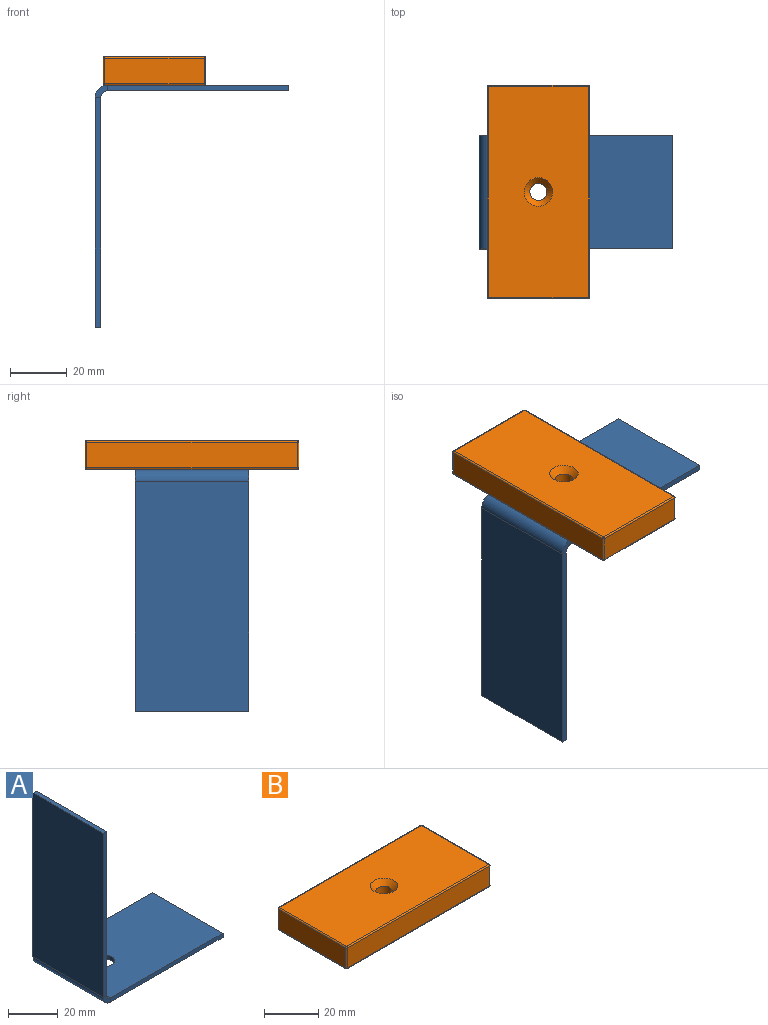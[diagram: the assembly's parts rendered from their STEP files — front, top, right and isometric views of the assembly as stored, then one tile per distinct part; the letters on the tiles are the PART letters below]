
ASSEMBLY  parts=2 mates=1
PART A: 15 faces, bbox 68x40x85 mm
  f0: plane 63.7x2mm, normal (0,1,0), area 127.4mm2, adj f3,f4,f5,f12
  f1: plane 63.7x2mm, normal (0,-1,0), area 127.4mm2, adj f3,f4,f5,f11
  f2: cylinder r=4mm len=8mm, axis (0,0,1), area 50.3mm2, adj f4,f5
  f3: plane 40x2mm, normal (1,0,0), area 80mm2, adj f0,f1,f4,f5
  f4: plane 63.7x40mm, normal (0,0,1), area 2497.7mm2, adj f0,f1,f2,f3,f14
  f5: plane 63.7x40mm, normal (0,0,-1), area 2497.7mm2, adj f0,f1,f2,f3,f13
  f6: plane 80.7x2mm, normal (0,1,0), area 161.4mm2, adj f7,f9,f10,f12
  f7: plane 40x2mm, normal (0,0,1), area 80mm2, adj f6,f8,f9,f10
  f8: plane 80.7x2mm, normal (0,-1,0), area 161.4mm2, adj f7,f9,f10,f11
  f9: plane 80.7x40mm, normal (1,0,0), area 3228mm2, adj f6,f7,f8,f14
  f10: plane 80.7x40mm, normal (-1,0,0), area 3228mm2, adj f6,f7,f8,f13
  f11: plane 4.3x4.3mm, normal (0,-1,0), area 10.4mm2, adj f1,f8,f13,f14
  f12: plane 4.3x4.3mm, normal (0,1,0), area 10.4mm2, adj f0,f6,f13,f14
  f13: cylinder r=4.3mm len=40mm, axis (0,-1,0), area 270.2mm2, adj f5,f10,f11,f12
  f14: cylinder r=2.3mm len=40mm, axis (0,-1,0), area 144.5mm2, adj f4,f9,f11,f12
PART B: 34 faces, bbox 75x36x10 mm
  f0: plane 74x9mm, normal (0,-1,0), area 666mm2, adj f14,f19,f22,f25
  f1: plane 35x9mm, normal (1,0,0), area 315mm2, adj f11,f20,f21,f25
  f2: plane 74x9mm, normal (0,1,0), area 666mm2, adj f6,f10,f11,f12
  f3: plane 35x9mm, normal (-1,0,0), area 315mm2, adj f6,f9,f13,f14
  f4: plane 74x35mm, normal (0,0,1), area 2511.5mm2, adj f9,f10,f19,f20,f33
  f5: plane 74x35mm, normal (0,0,-1), area 2536.6mm2, adj f12,f13,f21,f22,f27,f30,f32
  f6: cylinder r=0.5mm len=9mm, axis (0,0,-1), area 7.1mm2, adj f2,f3,f7,f8
  f7: sphere r=0.5mm, area 0.4mm2, adj f6,f9,f10
  f8: sphere r=0.5mm, area 0.4mm2, adj f6,f12,f13
  f9: cylinder r=0.5mm len=35mm, axis (0,1,0), area 27.5mm2, adj f3,f4,f7,f15
  f10: cylinder r=0.5mm len=74mm, axis (1,0,0), area 58.1mm2, adj f2,f4,f7,f16
  f11: cylinder r=0.5mm len=9mm, axis (0,0,-1), area 7.1mm2, adj f1,f2,f16,f17
  f12: cylinder r=0.5mm len=74mm, axis (-1,0,0), area 58.1mm2, adj f2,f5,f8,f17
  f13: cylinder r=0.5mm len=35mm, axis (0,-1,0), area 27.5mm2, adj f3,f5,f8,f18
  f14: cylinder r=0.5mm len=9mm, axis (0,0,-1), area 7.1mm2, adj f0,f3,f15,f18
  f15: sphere r=0.5mm, area 0.4mm2, adj f9,f14,f19
  f16: sphere r=0.5mm, area 0.4mm2, adj f10,f11,f20
  f17: sphere r=0.5mm, area 0.4mm2, adj f11,f12,f21
  f18: sphere r=0.5mm, area 0.4mm2, adj f13,f14,f22
  f19: cylinder r=0.5mm len=74mm, axis (-1,0,0), area 58.1mm2, adj f0,f4,f15,f23
  f20: cylinder r=0.5mm len=35mm, axis (0,-1,0), area 27.5mm2, adj f1,f4,f16,f23
  f21: cylinder r=0.5mm len=35mm, axis (0,1,0), area 27.5mm2, adj f1,f5,f17,f24
  f22: cylinder r=0.5mm len=74mm, axis (1,0,0), area 58.1mm2, adj f0,f5,f18,f24
  f23: sphere r=0.5mm, area 0.4mm2, adj f19,f20,f25
  f24: sphere r=0.5mm, area 0.4mm2, adj f21,f22,f25
  f25: cylinder r=0.5mm len=9mm, axis (0,0,-1), area 7.1mm2, adj f0,f1,f23,f24
  f26: cylinder r=1.5mm len=7.43mm, axis (0,0,-1), area 70mm2, adj f27,f28
  f27: cone r=1.5mm half-angle=41deg, axis (0,0,-1), area 8.4mm2, adj f5,f26
  f28: cone r=0mm half-angle=59deg, axis (0,0,-1), area 8.2mm2, adj f26
  f29: cylinder r=1.5mm len=7.43mm, axis (0,0,-1), area 70mm2, adj f30,f31
  f30: cone r=1.5mm half-angle=41deg, axis (0,0,-1), area 8.4mm2, adj f5,f29
  f31: cone r=0mm half-angle=59deg, axis (0,0,-1), area 8.2mm2, adj f29
  f32: cylinder r=3mm len=7.7mm, axis (0,0,1), area 145.1mm2, adj f5,f33
  f33: cone r=3mm half-angle=41deg, axis (0,0,1), area 76.6mm2, adj f4,f32
PLACE A rot(axis=(1,0,0),180deg) t=(63.63,59.12,63.88)mm
PLACE B rot(axis=(0,0,-1),90deg) t=(21.81,41.62,63.88)mm
MATE fastened A.f2 <-> B.f32  axis (0,0,1) through (39.81,79.12,63.88)mm
